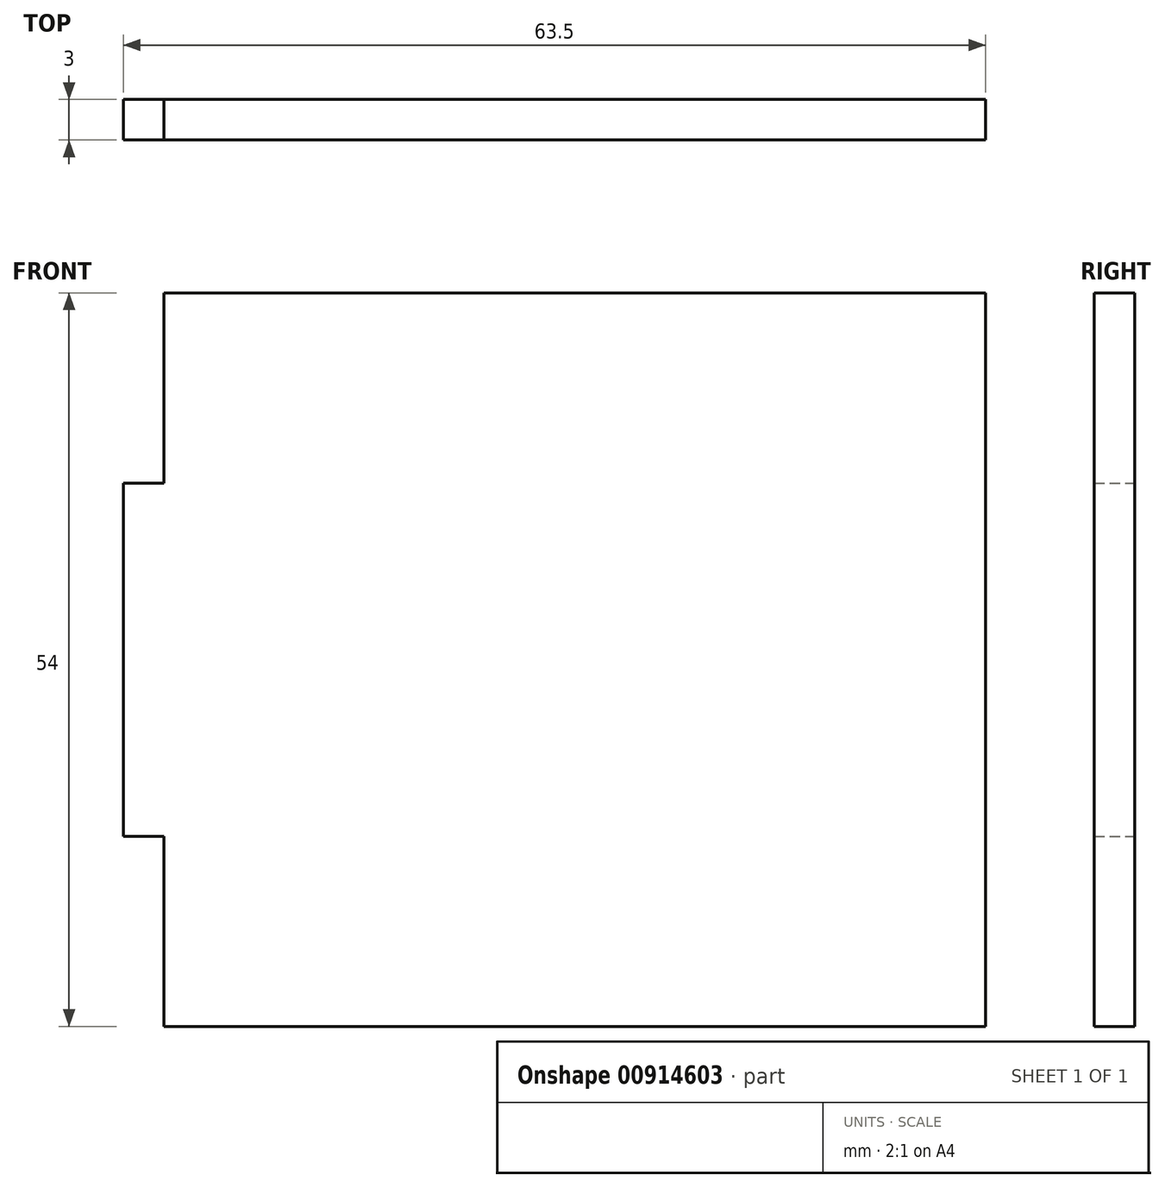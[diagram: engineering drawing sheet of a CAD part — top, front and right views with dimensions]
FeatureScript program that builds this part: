
annotation { "Feature Type Name" : "Feature", "Feature Type Description" : "" }
export const myFeature = defineFeature(function(context is Context, id is Id, definition is map)
    precondition{}
    {
        {
            var Q0;
            Q0=qCreatedBy(makeId("Front.planeOp"),FACE);
            var sketch = newSketch(context, id + "F0", { "sketchPlane" : qUnion([Q0])});
            skLineSegment(sketch, "E0.bottom", {"start": v(31.75, -27) * mm, "end": v(-28.75, -27) * mm});
            skLineSegment(sketch, "E0.top", {"start": v(31.75, 27) * mm, "end": v(-28.75, 27) * mm});
            skLineSegment(sketch, "E0.left", {"start": v(31.75, -27) * mm, "end": v(31.75, 27) * mm});
            skLineSegment(sketch, "E0.right", {"start": v(-31.75, -13) * mm, "end": v(-31.75, 13) * mm});
            skPoint(sketch, "E0.middle", {"position": v(0, 0) * mm});
            skLineSegment(sketch, "E1", {"start": v(-28.75, 27) * mm, "end": v(-28.75, 13) * mm});
            skLineSegment(sketch, "E2", {"start": v(-31.75, 13) * mm, "end": v(-28.75, 13) * mm});
            skLineSegment(sketch, "E3", {"start": v(-31.75, -13) * mm, "end": v(-28.75, -13) * mm});
            skPoint(sketch, "E4.orphan", {"position": v(-31.75, 27) * mm});
            skLineSegment(sketch, "E5.trimOffspring", {"start": v(-28.75, -13) * mm, "end": v(-28.75, -27) * mm});
            skPoint(sketch, "E6.orphan", {"position": v(-31.75, -27) * mm});
            skSolve(sketch);
        }
        {
            var Q0;
            Q0=makeQuery(id+"F0.imprint","IMPRINT",FACE,{"disambiguationData":[TD([[makeQuery(id+"F0.imprint","IMPRINT",EDGE,{"derivedFrom":sQuery(id+"F0.wireOp",EDGE,"E0.bottom")}),-1.0]])]});
            extrude(context, id + "F1", {"entities" : qUnion([Q0]), "depth" : 3 * mm, "offsetDistance" : 25 * mm});
        }
    });
